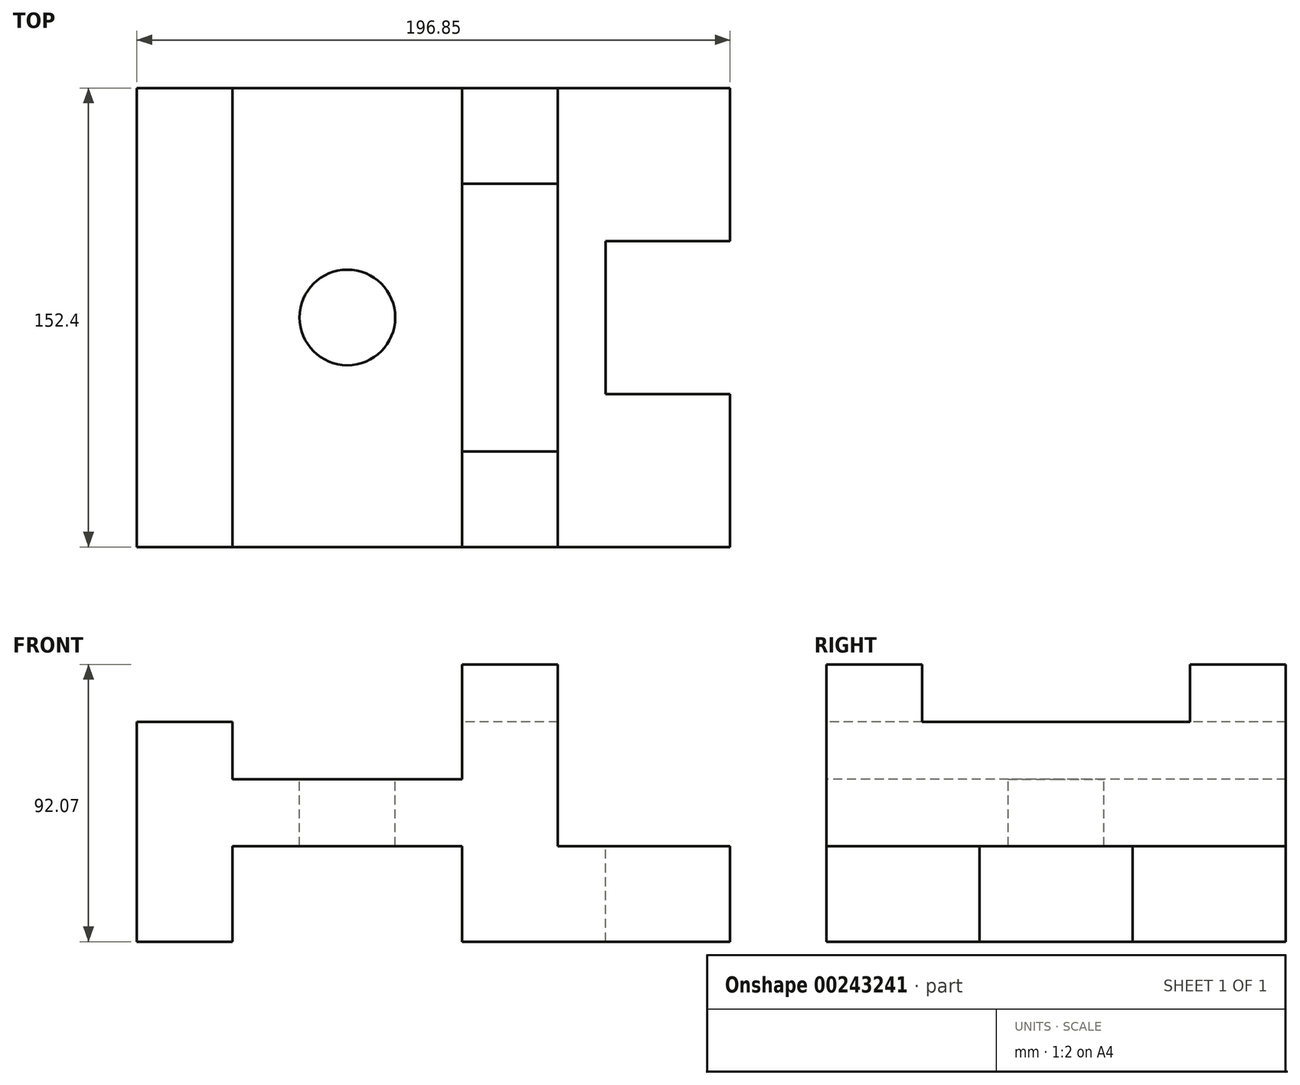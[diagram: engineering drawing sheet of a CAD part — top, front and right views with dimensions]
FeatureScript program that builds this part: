
annotation { "Feature Type Name" : "Feature", "Feature Type Description" : "" }
export const myFeature = defineFeature(function(context is Context, id is Id, definition is map)
    precondition{}
    {
        {
            var Q0;
            Q0=qCreatedBy(makeId("Top.planeOp"),FACE);
            var sketch = newSketch(context, id + "F0", { "sketchPlane" : qUnion([Q0])});
            skLineSegment(sketch, "E0.bottom", {"start": v(-127, 76.2) * mm, "end": v(127, 76.2) * mm});
            skLineSegment(sketch, "E0.top", {"start": v(-127, -76.2) * mm, "end": v(127, -76.2) * mm});
            skLineSegment(sketch, "E0.left", {"start": v(-127, 76.2) * mm, "end": v(-127, -76.2) * mm});
            skLineSegment(sketch, "E0.right", {"start": v(127, 76.2) * mm, "end": v(127, -76.2) * mm});
            skPoint(sketch, "E0.middle", {"position": v(0, 0) * mm});
            skLineSegment(sketch, "E1", {"start": v(-127, 76.2) * mm, "end": v(-127, 25.4) * mm});
            skLineSegment(sketch, "E2", {"start": v(-127, -76.2) * mm, "end": v(-127, -25.4) * mm});
            skLineSegment(sketch, "E3", {"start": v(-127, 25.4) * mm, "end": v(-85.73, 25.4) * mm});
            skLineSegment(sketch, "E4", {"start": v(-127, -25.4) * mm, "end": v(-85.73, -25.4) * mm});
            skLineSegment(sketch, "E5", {"start": v(-85.73, 25.4) * mm, "end": v(-85.73, -25.4) * mm});
            skLineSegment(sketch, "E6", {"start": v(-127, 76.2) * mm, "end": v(-69.85, 76.2) * mm});
            skLineSegment(sketch, "E7", {"start": v(-127, -76.2) * mm, "end": v(-69.85, -76.2) * mm});
            skLineSegment(sketch, "E8", {"start": v(-69.85, 76.2) * mm, "end": v(-69.85, -76.2) * mm});
            skLineSegment(sketch, "E9", {"start": v(-69.85, -76.2) * mm, "end": v(-38.1, -76.2) * mm});
            skLineSegment(sketch, "E10", {"start": v(-69.85, 76.2) * mm, "end": v(-38.1, 76.2) * mm});
            skLineSegment(sketch, "E11", {"start": v(-38.1, 76.2) * mm, "end": v(-38.1, -76.2) * mm});
            skLineSegment(sketch, "E12", {"start": v(-69.85, 76.2) * mm, "end": v(-69.85, 44.45) * mm});
            skLineSegment(sketch, "E13", {"start": v(-69.85, 44.45) * mm, "end": v(-38.1, 44.45) * mm});
            skLineSegment(sketch, "E14", {"start": v(-69.85, -76.2) * mm, "end": v(-69.85, -44.45) * mm});
            skLineSegment(sketch, "E15", {"start": v(-69.85, -44.45) * mm, "end": v(-38.1, -44.45) * mm});
            skLineSegment(sketch, "E16", {"start": v(0, 76.2) * mm, "end": v(0, -76.2) * mm});
            skLineSegment(sketch, "E17.MirrorCS", {"start": v(38.1, 76.2) * mm, "end": v(38.1, -76.2) * mm});
            skLineSegment(sketch, "E18.MirrorCS", {"start": v(69.85, 44.45) * mm, "end": v(38.1, 44.45) * mm});
            skLineSegment(sketch, "E19.MirrorCS", {"start": v(69.85, 76.2) * mm, "end": v(69.85, -76.2) * mm});
            skLineSegment(sketch, "E20.MirrorCS", {"start": v(69.85, -44.45) * mm, "end": v(38.1, -44.45) * mm});
            skLineSegment(sketch, "E21.MirrorCS", {"start": v(127, -25.4) * mm, "end": v(85.73, -25.4) * mm});
            skLineSegment(sketch, "E22.MirrorCS", {"start": v(127, 25.4) * mm, "end": v(85.73, 25.4) * mm});
            skLineSegment(sketch, "E23.MirrorCS", {"start": v(85.73, 25.4) * mm, "end": v(85.73, -25.4) * mm});
            skCircle(sketch, "E24", {"center": v(0, 0) * mm, "radius": 15.88 * mm});
            skSolve(sketch);
        }
        {
            var Q0;
            Q0=makeQuery(id+"F0.imprint","IMPRINT",FACE,{"disambiguationData":[TD([[makeQuery(id+"F0.imprint","IMPRINT",EDGE,{"derivedFrom":sQuery(id+"F0.wireOp",EDGE,"E1")}),1.0]])]});
            var Q1;
            Q1=makeQuery(id+"F0.imprint","IMPRINT",FACE,{"disambiguationData":[TD([[makeQuery(id+"F0.imprint","IMPRINT",EDGE,{"derivedFrom":sQuery(id+"F0.wireOp",EDGE,"E0.left")}),1.0]])]});
            var Q2;
            Q2=makeQuery(id+"F0.imprint","IMPRINT",FACE,{"disambiguationData":[TD([[makeQuery(id+"F0.imprint","IMPRINT",EDGE,{"derivedFrom":sQuery(id+"F0.wireOp",EDGE,"E8")}),1.0]])]});
            var Q3;
            {var subQ0=sQuery(id+"F0.wireOp",EDGE,"E10");Q3=makeQuery(id+"F0.imprint","IMPRINT",FACE,{"disambiguationData":[TD([[makeQuery(id+"F0.imprint","IMPRINT",EDGE,{"derivedFrom":subQ0}),-1.0]])]});}
            var Q4;
            {var subQ0=sQuery(id+"F0.wireOp",EDGE,"E9");Q4=makeQuery(id+"F0.imprint","IMPRINT",FACE,{"disambiguationData":[TD([[makeQuery(id+"F0.imprint","IMPRINT",EDGE,{"derivedFrom":subQ0}),1.0]])]});}
            var Q5;
            {var subQ0=sQuery(id+"F0.wireOp",EDGE,"E11");var subQ3=makeQuery(id+"F0.imprint","INTERSECT",VERTEX,{"derivedFrom":[subQ0,sQuery(id+"F0.wireOp",EDGE,"E13")]});Q5=makeQuery(id+"F0.imprint","IMPRINT",FACE,{"disambiguationData":[TD([[makeQuery(id+"F0.imprint","IMPRINT",EDGE,{"disambiguationData":[TD([[subQ3,-1.0]])],"derivedFrom":subQ0}),1.0]])]});}
            var Q6;
            {var subQ0=sQuery(id+"F0.wireOp",EDGE,"E24");var subQ1=sQuery(id+"F0.wireOp",EDGE,"E16");var subQ2=makeQuery(id+"F0.imprint","INTERSECT",VERTEX,{"disambiguationData":[OD(0.0)],"derivedFrom":[subQ1,subQ0]});Q6=makeQuery(id+"F0.imprint","IMPRINT",FACE,{"disambiguationData":[TD([[makeQuery(id+"F0.imprint","IMPRINT",EDGE,{"disambiguationData":[TD([[subQ2,-1.0]])],"derivedFrom":subQ1}),1.0]])]});}
            var Q7;
            {var subQ0=sQuery(id+"F0.wireOp",EDGE,"E24");var subQ1=sQuery(id+"F0.wireOp",EDGE,"E16");var subQ2=makeQuery(id+"F0.imprint","INTERSECT",VERTEX,{"disambiguationData":[OD(0.0)],"derivedFrom":[subQ1,subQ0]});Q7=makeQuery(id+"F0.imprint","IMPRINT",FACE,{"disambiguationData":[TD([[makeQuery(id+"F0.imprint","IMPRINT",EDGE,{"disambiguationData":[TD([[subQ2,-1.0]])],"derivedFrom":subQ1}),-1.0]])]});}
            var Q8;
            {var subQ0=sQuery(id+"F0.wireOp",EDGE,"E16");var subQ6=sQuery(id+"F0.wireOp",EDGE,"E0.bottom");var subQ7=makeQuery(id+"F0.imprint","INTERSECT",VERTEX,{"derivedFrom":[subQ6,subQ0]});Q8=makeQuery(id+"F0.imprint","IMPRINT",FACE,{"disambiguationData":[TD([[makeQuery(id+"F0.imprint","IMPRINT",EDGE,{"disambiguationData":[TD([[subQ7,-1.0]])],"derivedFrom":subQ6}),-1.0]])]});}
            var Q9;
            {var subQ0=sQuery(id+"F0.wireOp",EDGE,"E18.MirrorCS");Q9=makeQuery(id+"F0.imprint","IMPRINT",FACE,{"disambiguationData":[TD([[makeQuery(id+"F0.imprint","IMPRINT",EDGE,{"derivedFrom":subQ0}),1.0]])]});}
            var Q10;
            {var subQ5=sQuery(id+"F0.wireOp",EDGE,"E20.MirrorCS");Q10=makeQuery(id+"F0.imprint","IMPRINT",FACE,{"disambiguationData":[TD([[makeQuery(id+"F0.imprint","IMPRINT",EDGE,{"derivedFrom":subQ5}),1.0]])]});}
            var Q11;
            {var subQ5=sQuery(id+"F0.wireOp",EDGE,"E18.MirrorCS");Q11=makeQuery(id+"F0.imprint","IMPRINT",FACE,{"disambiguationData":[TD([[makeQuery(id+"F0.imprint","IMPRINT",EDGE,{"derivedFrom":subQ5}),-1.0]])]});}
            var Q12;
            {var subQ3=sQuery(id+"F0.wireOp",EDGE,"E21.MirrorCS");Q12=makeQuery(id+"F0.imprint","IMPRINT",FACE,{"disambiguationData":[TD([[makeQuery(id+"F0.imprint","IMPRINT",EDGE,{"derivedFrom":subQ3}),1.0]])]});}
            var Q13;
            {var subQ0=sQuery(id+"F0.wireOp",EDGE,"E21.MirrorCS");Q13=makeQuery(id+"F0.imprint","IMPRINT",FACE,{"disambiguationData":[TD([[makeQuery(id+"F0.imprint","IMPRINT",EDGE,{"derivedFrom":subQ0}),-1.0]])]});}
            extrude(context, id + "F1", {"entities" : qUnion([Q0, Q1, Q2, Q3, Q4, Q5, Q6, Q7, Q8, Q9, Q10, Q11, Q12, Q13]), "oppositeDirection" : true, "depth" : 31.75 * mm});
        }
        {
            var Q0;
            Q0=makeQuery(id+"F0.imprint","IMPRINT",FACE,{"disambiguationData":[TD([[makeQuery(id+"F0.imprint","IMPRINT",EDGE,{"derivedFrom":sQuery(id+"F0.wireOp",EDGE,"E0.left")}),1.0]])]});
            var Q1;
            {var subQ0=sQuery(id+"F0.wireOp",EDGE,"E21.MirrorCS");Q1=makeQuery(id+"F0.imprint","IMPRINT",FACE,{"disambiguationData":[TD([[makeQuery(id+"F0.imprint","IMPRINT",EDGE,{"derivedFrom":subQ0}),-1.0]])]});}
            extrude(context, id + "F2", {"entities" : qUnion([Q0, Q1]), "operationType" : NewBodyOperationType.REMOVE, "endBound" : BoundingType.THROUGH_ALL, "oppositeDirection" : true, "depth" : 25.4 * mm});
        }
        {
            var Q0;
            {var subQ0=sQuery(id+"F0.wireOp",EDGE,"E11");var subQ3=makeQuery(id+"F0.imprint","INTERSECT",VERTEX,{"derivedFrom":[subQ0,sQuery(id+"F0.wireOp",EDGE,"E13")]});Q0=makeQuery(id+"F0.imprint","IMPRINT",FACE,{"disambiguationData":[TD([[makeQuery(id+"F0.imprint","IMPRINT",EDGE,{"disambiguationData":[TD([[subQ3,-1.0]])],"derivedFrom":subQ0}),1.0]])]});}
            var Q1;
            {var subQ0=sQuery(id+"F0.wireOp",EDGE,"E16");var subQ6=sQuery(id+"F0.wireOp",EDGE,"E0.bottom");var subQ7=makeQuery(id+"F0.imprint","INTERSECT",VERTEX,{"derivedFrom":[subQ6,subQ0]});Q1=makeQuery(id+"F0.imprint","IMPRINT",FACE,{"disambiguationData":[TD([[makeQuery(id+"F0.imprint","IMPRINT",EDGE,{"disambiguationData":[TD([[subQ7,-1.0]])],"derivedFrom":subQ6}),-1.0]])]});}
            extrude(context, id + "F3", {"entities" : qUnion([Q0, Q1]), "operationType" : NewBodyOperationType.ADD, "depth" : 22.22 * mm});
        }
        {
            var Q0;
            {var subQ0=sQuery(id+"F0.wireOp",EDGE,"E10");Q0=makeQuery(id+"F0.imprint","IMPRINT",FACE,{"disambiguationData":[TD([[makeQuery(id+"F0.imprint","IMPRINT",EDGE,{"derivedFrom":subQ0}),-1.0]])]});}
            var Q1;
            {var subQ0=sQuery(id+"F0.wireOp",EDGE,"E9");Q1=makeQuery(id+"F0.imprint","IMPRINT",FACE,{"disambiguationData":[TD([[makeQuery(id+"F0.imprint","IMPRINT",EDGE,{"derivedFrom":subQ0}),1.0]])]});}
            var Q2;
            {var subQ5=sQuery(id+"F0.wireOp",EDGE,"E18.MirrorCS");Q2=makeQuery(id+"F0.imprint","IMPRINT",FACE,{"disambiguationData":[TD([[makeQuery(id+"F0.imprint","IMPRINT",EDGE,{"derivedFrom":subQ5}),-1.0]])]});}
            var Q3;
            {var subQ5=sQuery(id+"F0.wireOp",EDGE,"E20.MirrorCS");Q3=makeQuery(id+"F0.imprint","IMPRINT",FACE,{"disambiguationData":[TD([[makeQuery(id+"F0.imprint","IMPRINT",EDGE,{"derivedFrom":subQ5}),1.0]])]});}
            extrude(context, id + "F4", {"entities" : qUnion([Q0, Q1, Q2, Q3]), "operationType" : NewBodyOperationType.ADD, "depth" : 60.32 * mm});
        }
        {
            var Q0;
            Q0=makeQuery(id+"F0.imprint","IMPRINT",FACE,{"disambiguationData":[TD([[makeQuery(id+"F0.imprint","IMPRINT",EDGE,{"derivedFrom":sQuery(id+"F0.wireOp",EDGE,"E8")}),1.0]])]});
            var Q1;
            {var subQ0=sQuery(id+"F0.wireOp",EDGE,"E18.MirrorCS");Q1=makeQuery(id+"F0.imprint","IMPRINT",FACE,{"disambiguationData":[TD([[makeQuery(id+"F0.imprint","IMPRINT",EDGE,{"derivedFrom":subQ0}),1.0]])]});}
            extrude(context, id + "F5", {"entities" : qUnion([Q0, Q1]), "operationType" : NewBodyOperationType.ADD, "depth" : 41.27 * mm});
        }
        {
            var Q0;
            {var subQ0=sQuery(id+"F0.wireOp",EDGE,"E24");var subQ1=sQuery(id+"F0.wireOp",EDGE,"E16");var subQ2=makeQuery(id+"F0.imprint","INTERSECT",VERTEX,{"disambiguationData":[OD(0.0)],"derivedFrom":[subQ1,subQ0]});Q0=makeQuery(id+"F0.imprint","IMPRINT",FACE,{"disambiguationData":[TD([[makeQuery(id+"F0.imprint","IMPRINT",EDGE,{"disambiguationData":[TD([[subQ2,-1.0]])],"derivedFrom":subQ1}),-1.0]])]});}
            var Q1;
            {var subQ0=sQuery(id+"F0.wireOp",EDGE,"E24");var subQ1=sQuery(id+"F0.wireOp",EDGE,"E16");var subQ2=makeQuery(id+"F0.imprint","INTERSECT",VERTEX,{"disambiguationData":[OD(0.0)],"derivedFrom":[subQ1,subQ0]});Q1=makeQuery(id+"F0.imprint","IMPRINT",FACE,{"disambiguationData":[TD([[makeQuery(id+"F0.imprint","IMPRINT",EDGE,{"disambiguationData":[TD([[subQ2,-1.0]])],"derivedFrom":subQ1}),1.0]])]});}
            extrude(context, id + "F6", {"entities" : qUnion([Q0, Q1]), "operationType" : NewBodyOperationType.REMOVE, "endBound" : BoundingType.THROUGH_ALL, "oppositeDirection" : true, "depth" : 25.4 * mm});
        }
    });
